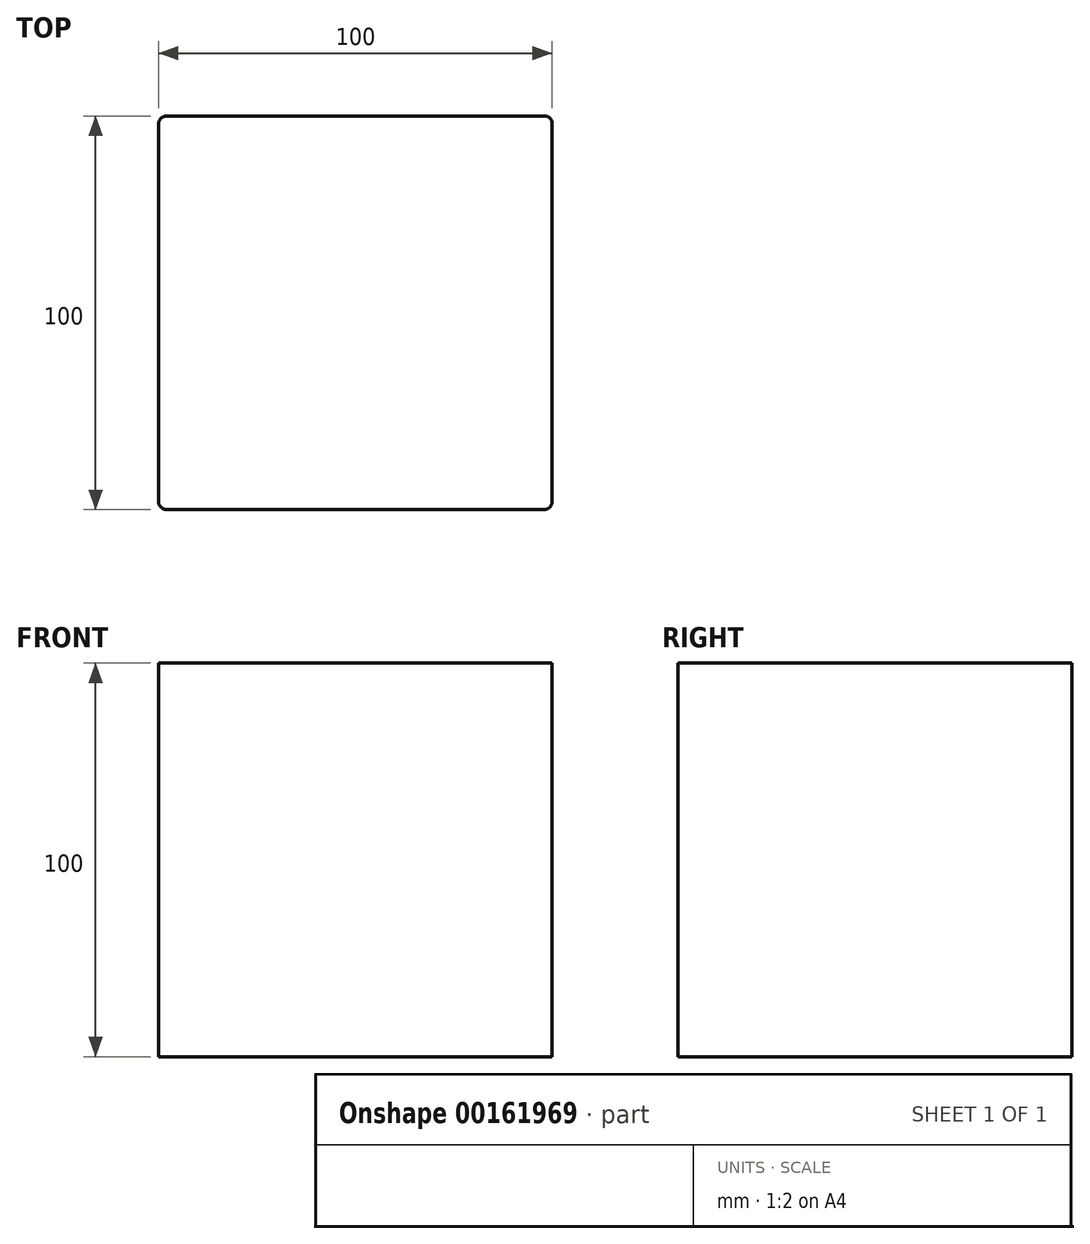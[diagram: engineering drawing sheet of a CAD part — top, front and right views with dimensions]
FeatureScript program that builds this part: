
annotation { "Feature Type Name" : "Feature", "Feature Type Description" : "" }
export const myFeature = defineFeature(function(context is Context, id is Id, definition is map)
    precondition{}
    {
        {
            var Q0;
            Q0=qCreatedBy(makeId("Front.planeOp"),FACE);
            var sketch = newSketch(context, id + "F0", { "sketchPlane" : qUnion([Q0])});
            skLineSegment(sketch, "E0.bottom", {"start": v(0, 0) * mm, "end": v(100, 0) * mm});
            skLineSegment(sketch, "E0.top", {"start": v(0, 100) * mm, "end": v(100, 100) * mm});
            skLineSegment(sketch, "E0.left", {"start": v(0, 0) * mm, "end": v(0, 100) * mm});
            skLineSegment(sketch, "E0.right", {"start": v(100, 0) * mm, "end": v(100, 100) * mm});
            skSolve(sketch);
        }
        {
            var Q0;
            Q0 = qSketchRegion(id + "F0", true);
            extrude(context, id + "F1", {"entities" : qUnion([Q0]), "depth" : 100 * mm});
        }
        {
            var Q0;
            Q0=makeQuery(id+"F1.opExtrude","CAP_EDGE",EDGE,{"disambiguationData":[OSD([sQuery(id+"F0.wireOp",EDGE,"E0.right")])],"isStart":false});
            var Q1;
            Q1=makeQuery(id+"F1.opExtrude","CAP_EDGE",EDGE,{"disambiguationData":[OSD([sQuery(id+"F0.wireOp",EDGE,"E0.right")])],"isStart":true});
            var Q2;
            Q2=makeQuery(id+"F1.opExtrude","CAP_EDGE",EDGE,{"disambiguationData":[OSD([sQuery(id+"F0.wireOp",EDGE,"E0.left")])],"isStart":true});
            var Q3;
            Q3=makeQuery(id+"F1.opExtrude","CAP_EDGE",EDGE,{"disambiguationData":[OSD([sQuery(id+"F0.wireOp",EDGE,"E0.left")])],"isStart":false});
            fillet(context, id + "F2", {"entities" : qUnion([Q0, Q1, Q2, Q3]), "radius" : 2 * mm, "tangentPropagation" : true, "allowEdgeOverflow" : false});
        }
    });
